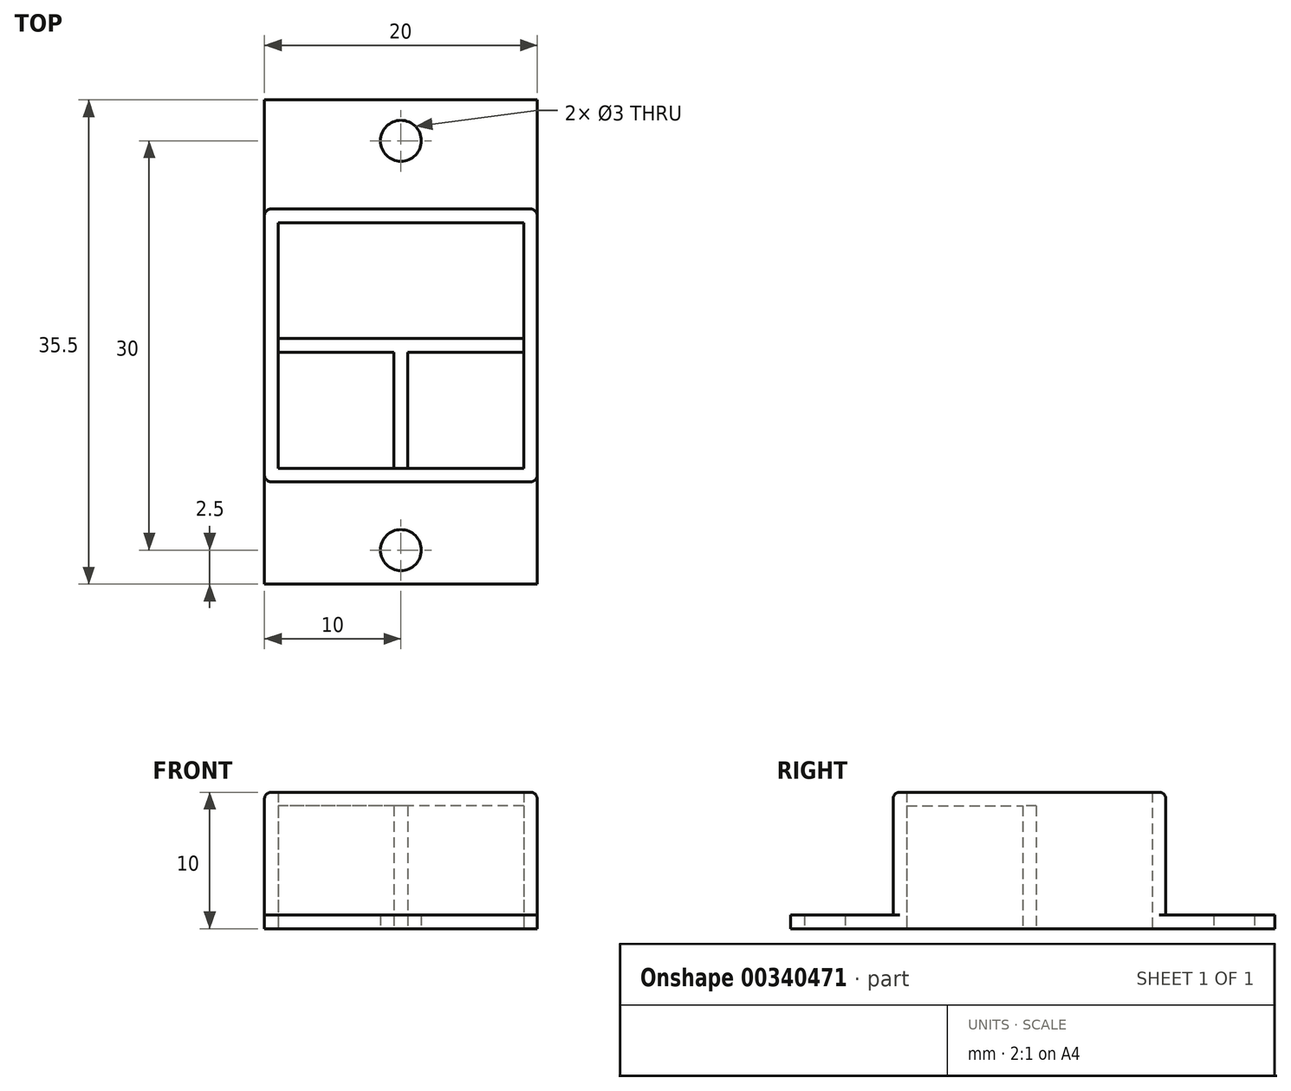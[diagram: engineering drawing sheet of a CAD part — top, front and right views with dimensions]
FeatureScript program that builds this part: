
annotation { "Feature Type Name" : "Feature", "Feature Type Description" : "" }
export const myFeature = defineFeature(function(context is Context, id is Id, definition is map)
    precondition{}
    {
        {
            var Q0;
            Q0=qCreatedBy(makeId("Top.planeOp"),FACE);
            var sketch = newSketch(context, id + "F0", { "sketchPlane" : qUnion([Q0])});
            skPoint(sketch, "E0.middle", {"position": v(0, 0) * mm});
            skLineSegment(sketch, "E1.bottom", {"start": v(10, -10) * mm, "end": v(-10, -10) * mm});
            skLineSegment(sketch, "E1.top", {"start": v(10, 10) * mm, "end": v(-10, 10) * mm});
            skLineSegment(sketch, "E1.left", {"start": v(10, -10) * mm, "end": v(10, 10) * mm});
            skLineSegment(sketch, "E1.right", {"start": v(-10, -10) * mm, "end": v(-10, 10) * mm});
            skSolve(sketch);
        }
        {
            var Q0;
            Q0=makeQuery(id+"F0.imprint","IMPRINT",FACE,{"disambiguationData":[TD([[makeQuery(id+"F0.imprint","IMPRINT",EDGE,{"derivedFrom":sQuery(id+"F0.wireOp",EDGE,"E1.bottom")}),-1.0]])]});
            extrude(context, id + "F1", {"entities" : qUnion([Q0]), "depth" : 10 * mm});
        }
        {
            var Q0;
            Q0=makeQuery(id+"F1.opExtrude","CAP_FACE",FACE,{"disambiguationData":[OSD([sQuery(id+"F0.wireOp",EDGE,"E1.bottom"),sQuery(id+"F0.wireOp",EDGE,"E1.top"),sQuery(id+"F0.wireOp",EDGE,"E1.left"),sQuery(id+"F0.wireOp",EDGE,"E1.right")])],"isStart":true});
            shell(context, id + "F2", {"entities" : qUnion([Q0]), "thickness" : 1 * mm});
        }
        {
            var Q0;
            Q0=qCreatedBy(makeId("Top.planeOp"),FACE);
            var sketch = newSketch(context, id + "F3", { "sketchPlane" : qUnion([Q0])});
            skLineSegment(sketch, "E2.bottom", {"start": v(0.5, -9) * mm, "end": v(-0.5, -9) * mm});
            skLineSegment(sketch, "E2.left", {"start": v(0.5, -9) * mm, "end": v(0.5, -0.5) * mm});
            skLineSegment(sketch, "E2.right", {"start": v(-0.5, -9) * mm, "end": v(-0.5, -0.5) * mm});
            skLineSegment(sketch, "E3.bottom", {"start": v(9, 0.5) * mm, "end": v(0.5, 0.5) * mm});
            skLineSegment(sketch, "E3.top", {"start": v(9, -0.5) * mm, "end": v(0.5, -0.5) * mm});
            skLineSegment(sketch, "E3.left", {"start": v(9, 0.5) * mm, "end": v(9, -0.5) * mm});
            skLineSegment(sketch, "E3.right", {"start": v(-9, 0.5) * mm, "end": v(-9, -0.5) * mm});
            skLineSegment(sketch, "E4.trimOffspring", {"start": v(-0.5, -0.5) * mm, "end": v(-9, -0.5) * mm});
            skLineSegment(sketch, "E5.trimOffspring", {"start": v(-0.5, 0.5) * mm, "end": v(-9, 0.5) * mm});
            skLineSegment(sketch, "E6", {"start": v(-0.5, 0.5) * mm, "end": v(0.5, 0.5) * mm});
            skSolve(sketch);
        }
        {
            var Q0;
            Q0=qSketchRegion(id+"F3",true);
            extrude(context, id + "F4", {"entities" : qUnion([Q0]), "operationType" : NewBodyOperationType.ADD, "depth" : 9 * mm});
        }
        {
            var Q0;
            Q0=qCreatedBy(makeId("Top.planeOp"),FACE);
            var sketch = newSketch(context, id + "F5", { "sketchPlane" : qUnion([Q0])});
            skLineSegment(sketch, "E7.bottom", {"start": v(-10, -9.5) * mm, "end": v(10, -9.5) * mm});
            skLineSegment(sketch, "E7.top", {"start": v(-10, -17.5) * mm, "end": v(10, -17.5) * mm});
            skLineSegment(sketch, "E7.left", {"start": v(-10, -9.5) * mm, "end": v(-10, -17.5) * mm});
            skLineSegment(sketch, "E7.right", {"start": v(10, -9.5) * mm, "end": v(10, -17.5) * mm});
            skLineSegment(sketch, "E8.bottom", {"start": v(-10, 10) * mm, "end": v(10, 10) * mm});
            skLineSegment(sketch, "E8.top", {"start": v(-10, 18) * mm, "end": v(10, 18) * mm});
            skLineSegment(sketch, "E8.left", {"start": v(-10, 10) * mm, "end": v(-10, 18) * mm});
            skLineSegment(sketch, "E8.right", {"start": v(10, 10) * mm, "end": v(10, 18) * mm});
            skLineSegment(sketch, "E9.bottom", {"start": v(-10, -9.5) * mm, "end": v(-13, -9.5) * mm, "construction": true});
            skLineSegment(sketch, "E9.top", {"start": v(-10, 10) * mm, "end": v(-13, 10) * mm, "construction": true});
            skLineSegment(sketch, "E9.left", {"start": v(-10, -9.5) * mm, "end": v(-10, 10) * mm});
            skLineSegment(sketch, "E9.right", {"start": v(-13, -9.5) * mm, "end": v(-13, 10) * mm, "construction": true});
            skLineSegment(sketch, "E10.bottom", {"start": v(10, -9.5) * mm, "end": v(13, -9.5) * mm, "construction": true});
            skLineSegment(sketch, "E10.top", {"start": v(10, 10) * mm, "end": v(13, 10) * mm, "construction": true});
            skLineSegment(sketch, "E10.left", {"start": v(10, -9.5) * mm, "end": v(10, 10) * mm});
            skLineSegment(sketch, "E10.right", {"start": v(13, -9.5) * mm, "end": v(13, 10) * mm, "construction": true});
            skCircle(sketch, "E11", {"center": v(0, 15) * mm, "radius": 1.5 * mm});
            skCircle(sketch, "E12", {"center": v(0, -15) * mm, "radius": 1.5 * mm});
            skSolve(sketch);
        }
        {
            var Q0;
            Q0=makeQuery(id+"F5.imprint","IMPRINT",FACE,{"disambiguationData":[TD([[makeQuery(id+"F5.imprint","IMPRINT",EDGE,{"derivedFrom":sQuery(id+"F5.wireOp",EDGE,"E9.bottom")}),-1.0]])]});
            var Q1;
            Q1=makeQuery(id+"F5.imprint","IMPRINT",FACE,{"disambiguationData":[TD([[makeQuery(id+"F5.imprint","IMPRINT",EDGE,{"derivedFrom":sQuery(id+"F5.wireOp",EDGE,"E7.bottom")}),-1.0]])]});
            var Q2;
            Q2=makeQuery(id+"F5.imprint","IMPRINT",FACE,{"disambiguationData":[TD([[makeQuery(id+"F5.imprint","IMPRINT",EDGE,{"derivedFrom":sQuery(id+"F5.wireOp",EDGE,"E10.bottom")}),1.0]])]});
            var Q3;
            Q3=makeQuery(id+"F5.imprint","IMPRINT",FACE,{"disambiguationData":[TD([[makeQuery(id+"F5.imprint","IMPRINT",EDGE,{"derivedFrom":sQuery(id+"F5.wireOp",EDGE,"E8.bottom")}),1.0]])]});
            extrude(context, id + "F6", {"entities" : qUnion([Q0, Q1, Q2, Q3]), "operationType" : NewBodyOperationType.ADD, "depth" : 1 * mm});
        }
        {
            var Q0;
            Q0=makeQuery(id+"F1.opExtrude","CAP_FACE",FACE,{"disambiguationData":[OSD([sQuery(id+"F0.wireOp",EDGE,"E1.bottom"),sQuery(id+"F0.wireOp",EDGE,"E1.top"),sQuery(id+"F0.wireOp",EDGE,"E1.left"),sQuery(id+"F0.wireOp",EDGE,"E1.right")])],"isStart":false});
            var sketch = newSketch(context, id + "F7", { "sketchPlane" : qUnion([Q0])});
            skLineSegment(sketch, "E13.bottom", {"start": v(9, 9) * mm, "end": v(-9, 9) * mm});
            skLineSegment(sketch, "E13.top", {"start": v(9, -9) * mm, "end": v(-9, -9) * mm});
            skLineSegment(sketch, "E13.left", {"start": v(9, 9) * mm, "end": v(9, -9) * mm});
            skLineSegment(sketch, "E13.right", {"start": v(-9, 9) * mm, "end": v(-9, -9) * mm});
            skPoint(sketch, "E13.middle", {"position": v(0, 0) * mm});
            skSolve(sketch);
        }
        {
            var Q0;
            Q0=qSketchRegion(id+"F7",true);
            extrude(context, id + "F8", {"entities" : qUnion([Q0]), "operationType" : NewBodyOperationType.REMOVE, "oppositeDirection" : true, "depth" : 1 * mm});
        }
        {
            var Q0;
            Q0=makeQuery(id+"F1.opExtrude","CAP_EDGE",EDGE,{"disambiguationData":[OSD([sQuery(id+"F0.wireOp",EDGE,"E1.left")])],"isStart":false});
            var Q1;
            Q1=makeQuery(id+"F1.opExtrude","CAP_EDGE",EDGE,{"disambiguationData":[OSD([sQuery(id+"F0.wireOp",EDGE,"E1.bottom")])],"isStart":false});
            var Q2;
            Q2=makeQuery(id+"F1.opExtrude","SWEPT_EDGE",EDGE,{"disambiguationData":[OSD([sQuery(id+"F0.wireOp",EDGE,"E1.bottom"),sQuery(id+"F0.wireOp",EDGE,"E1.left")])]});
            var Q3;
            Q3=makeQuery(id+"F1.opExtrude","SWEPT_EDGE",EDGE,{"disambiguationData":[OSD([sQuery(id+"F0.wireOp",EDGE,"E1.bottom"),sQuery(id+"F0.wireOp",EDGE,"E1.right")])]});
            var Q4;
            Q4=makeQuery(id+"F1.opExtrude","SWEPT_EDGE",EDGE,{"disambiguationData":[OSD([sQuery(id+"F0.wireOp",EDGE,"E1.top"),sQuery(id+"F0.wireOp",EDGE,"E1.left")])]});
            var Q5;
            Q5=makeQuery(id+"F1.opExtrude","SWEPT_EDGE",EDGE,{"disambiguationData":[OSD([sQuery(id+"F0.wireOp",EDGE,"E1.top"),sQuery(id+"F0.wireOp",EDGE,"E1.right")])]});
            var Q6;
            Q6=makeQuery(id+"F1.opExtrude","CAP_EDGE",EDGE,{"disambiguationData":[OSD([sQuery(id+"F0.wireOp",EDGE,"E1.top")])],"isStart":false});
            var Q7;
            Q7=makeQuery(id+"F1.opExtrude","CAP_EDGE",EDGE,{"disambiguationData":[OSD([sQuery(id+"F0.wireOp",EDGE,"E1.right")])],"isStart":false});
            fillet(context, id + "F9", {"entities" : qUnion([Q0, Q1, Q2, Q3, Q4, Q5, Q6, Q7]), "radius" : 0.5 * mm, "tangentPropagation" : true, "allowEdgeOverflow" : false});
        }
    });
